# Revit family: QF_BOURGEAT_Self_5GN_et_6GN_vitrine_refrigeree_3nv
name_source: partatom
category: Equipement spécialisé
revit_build: Autodesk Revit 2015 (Build: 20140606_1530(x64)
units: mm (PartAtom-declared; Revit-internal decimal feet)

## types (36) — shared parameters
Certification = NF alimentaire
Charge max = 200.00 kg
Classe_climatique = 3
Fabricant = BOURGEAT
Fréquence = 50 Hz
Hauteur hors tout = 1800 mm  [stored 5.90551 ft]
Indice de protection = 21
Nature isolant = polyurethane
Niveau Sonore = 60dBa
Phase = 2
Profondeur hors tout = 820 mm  [stored 2.69029 ft]
Spécification du Fabricant = vitrine réfrigérée 3 niveaux OASIS
Tension = 230 V
Type Fluide Frigorigène = R404a
URL catalogue = http://www.bourgeat.fr

## per-type parameters (varying)
| type | Etageres | Intensité nominale | Longueur hors tout | Modèle | Pieds | Poids net à vide | Puissance frigorifique | Puissance électrique  | Roues | cuve_plate | lg_porte_groupe_froid | lg_vitrine | profondeur_cuve | reserve |
| 6GN_baie_libre_cuve_plate | Non | 11 A | 2335 mm  [stored 7.66076 ft] | 853106 | Oui | 380.00 kg | 2126W | 2500 W | Non | Oui | 790 mm  [stored 2.59186 ft] | 2200 mm | 0 mm  [stored 0 ft] | Non |
| 6GN_baie_libre_cuve90 | Non | 11 A | 2335 mm  [stored 7.66076 ft] | 853196 | Oui | 380.00 kg | 2126W | 2500 W | Non | Non | 790 mm  [stored 2.59186 ft] | 2200 mm | 90 mm  [stored 0.295276 ft] | Non |
| 6GN_reserve_cuve_plate | Non | 12 A | 2335 mm  [stored 7.66076 ft] | 853406 | Oui | 380.00 kg | 2126W | 2700 W | Non | Oui | 790 mm  [stored 2.59186 ft] | 2200 mm | 0 mm  [stored 0 ft] | Oui |
| 6GN_reserve_cuve90 | Non | 12 A | 2335 mm  [stored 7.66076 ft] | 853496 | Oui | 380.00 kg | 2126W | 2700 W | Non | Non | 790 mm  [stored 2.59186 ft] | 2200 mm | 90 mm  [stored 0.295276 ft] | Oui |
| 6GN_baie_libre_cuve_plate_roues | Non | 11 A | 2335 mm  [stored 7.66076 ft] | 853106 + 854950 | Non | 380.00 kg | 2126W | 2500 W | Oui | Oui | 790 mm  [stored 2.59186 ft] | 2200 mm | 0 mm  [stored 0 ft] | Non |
| 6GN_baie_libre_cuve90_roues | Non | 11 A | 2335 mm  [stored 7.66076 ft] | 853196 + 854950 | Non | 380.00 kg | 2126W | 2500 W | Oui | Non | 790 mm  [stored 2.59186 ft] | 2200 mm | 90 mm  [stored 0.295276 ft] | Non |
| 6GN_reserve_cuve_plate_roues | Non | 12 A | 2335 mm  [stored 7.66076 ft] | 853406 + 854950 | Non | 380.00 kg | 2126W | 2700 W | Oui | Oui | 790 mm  [stored 2.59186 ft] | 2200 mm | 0 mm  [stored 0 ft] | Oui |
| 6GN_reserve_cuve90_roues | Non | 12 A | 2335 mm  [stored 7.66076 ft] | 853496 + 854950 | Non | 380.00 kg | 2126W | 2700 W | Oui | Oui | 790 mm  [stored 2.59186 ft] | 2200 mm | 90 mm  [stored 0.295276 ft] | Oui |
| 6GN_baie_libre_cuve_plate_etageres | Oui | 11 A | 2335 mm  [stored 7.66076 ft] | 853106 + 854926 | Oui | 380.00 kg | 2126W | 2500 W | Non | Oui | 790 mm  [stored 2.59186 ft] | 2200 mm | 0 mm  [stored 0 ft] | Non |
| 6GN_baie_libre_cuve90_etageres | Oui | 11 A | 2335 mm  [stored 7.66076 ft] | 853196 + 854926 | Oui | 380.00 kg | 2126W | 2500 W | Non | Non | 790 mm  [stored 2.59186 ft] | 2200 mm | 90 mm  [stored 0.295276 ft] | Non |
| 6GN_baie_libre_cuve_plate_etageres_roues | Oui | 11 A | 2335 mm  [stored 7.66076 ft] | 853106 + 854926 + 854950 | Non | 380.00 kg | 2126W | 2500 W | Oui | Oui | 790 mm  [stored 2.59186 ft] | 2200 mm | 0 mm  [stored 0 ft] | Non |
| 6GN_baie_libre_cuve90_etageres_roues | Oui | 11 A | 2335 mm  [stored 7.66076 ft] | 853196 + 854926 + 854950 | Non | 380.00 kg | 2126W | 2500 W | Oui | Non | 790 mm  [stored 2.59186 ft] | 2200 mm | 90 mm  [stored 0.295276 ft] | Non |
| 5GN_baie_libre_cuve_plate | Non | 10 A | 2010 mm  [stored 6.59449 ft] | 853105 | Oui | 355.00 kg | 1440W | 2400 W | Non | Oui | 591 mm  [stored 1.93898 ft] | 1875 mm  [stored 6.15157 ft] | 0 mm  [stored 0 ft] | Non |
| 5GN_reserve_cuve_plate | Non | 11 A | 2010 mm  [stored 6.59449 ft] | 853405 | Oui | 355.00 kg | 1727W | 2500 W | Non | Oui | 591 mm  [stored 1.93898 ft] | 1875 mm  [stored 6.15157 ft] | 0 mm  [stored 0 ft] | Oui |
| 5GN_baie_libre_cuve90 | Non | 10 A | 2010 mm  [stored 6.59449 ft] | 853195 | Oui | 355.00 kg | 1440W | 2400 W | Non | Non | 591 mm  [stored 1.93898 ft] | 1875 mm  [stored 6.15157 ft] | 90 mm  [stored 0.295276 ft] | Non |
| 5GN_reserve_cuve90 | Non | 11 A | 2010 mm  [stored 6.59449 ft] | 853495 | Oui | 355.00 kg | 1727W | 2500 W | Non | Oui | 591 mm  [stored 1.93898 ft] | 1875 mm  [stored 6.15157 ft] | 90 mm  [stored 0.295276 ft] | Oui |
| 5GN_baie_libre_cuve_plate_roues | Non | 10 A | 2010 mm  [stored 6.59449 ft] | 853105 + 854950 | Non | 355.00 kg | 1440W | 2400 W | Oui | Oui | 591 mm  [stored 1.93898 ft] | 1875 mm  [stored 6.15157 ft] | 0 mm  [stored 0 ft] | Non |
| 5GN_baie_libre_cuve90_roues | Non | 10 A | 2010 mm  [stored 6.59449 ft] | 853195 + 854950 | Non | 355.00 kg | 1440W | 2400 W | Oui | Non | 591 mm  [stored 1.93898 ft] | 1875 mm  [stored 6.15157 ft] | 90 mm  [stored 0.295276 ft] | Non |
| 5GN_reserve_cuve_plate_roues | Non | 11 A | 2010 mm  [stored 6.59449 ft] | 853405 | Oui | 355.00 kg | 1727W | 2500 W | Non | Oui | 591 mm  [stored 1.93898 ft] | 1875 mm  [stored 6.15157 ft] | 0 mm  [stored 0 ft] | Oui |
| 5GN_reserve_cuve90_roues | Non | 11 A | 2010 mm  [stored 6.59449 ft] | 853495 + 854950 | Non | 355.00 kg | 1727W | 2500 W | Oui | Non | 591 mm  [stored 1.93898 ft] | 1875 mm  [stored 6.15157 ft] | 90 mm  [stored 0.295276 ft] | Oui |
| 5GN_baie_libre_cuve_plate_etageres | Oui | 10 A | 2010 mm  [stored 6.59449 ft] | 853105 + 854925 | Oui | 355.00 kg | 1440W | 2400 W | Non | Oui | 591 mm  [stored 1.93898 ft] | 1875 mm  [stored 6.15157 ft] | 0 mm  [stored 0 ft] | Non |
| 5GN_baie_libre_cuve90_etageres | Oui | 10 A | 2010 mm  [stored 6.59449 ft] | 853195 + 854925 | Oui | 355.00 kg | 1440W | 2400 W | Non | Non | 591 mm  [stored 1.93898 ft] | 1875 mm  [stored 6.15157 ft] | 90 mm  [stored 0.295276 ft] | Non |
| 5GN_baie_libre_cuve_plate_etageres_roues | Oui | 10 A | 2010 mm  [stored 6.59449 ft] | 853105 + 854925 + 854950 | Non | 355.00 kg | 1440W | 2400 W | Oui | Oui | 591 mm  [stored 1.93898 ft] | 1875 mm  [stored 6.15157 ft] | 0 mm  [stored 0 ft] | Non |
| 5GN_baie_libre_cuve90_etageres_roues | Oui | 10 A | 2010 mm  [stored 6.59449 ft] | 853195 + 854925 | Non | 355.00 kg | 1440W | 2400 W | Oui | Non | 591 mm  [stored 1.93898 ft] | 1875 mm  [stored 6.15157 ft] | 90 mm  [stored 0.295276 ft] | Non |
| 5GN_baie_libre_cuve_30 | Non | 10 A | 2010 mm  [stored 6.59449 ft] | 853205 | Oui | 355.00 kg | 1440W | 2400 W | Non | Oui | 591 mm  [stored 1.93898 ft] | 1875 mm  [stored 6.15157 ft] | 30 mm  [stored 0.0984252 ft] | Non |
| 5GN_baie_libre_cuve_30_etageres | Oui | 10 A | 2010 mm  [stored 6.59449 ft] | 853205 + 854925 | Oui | 355.00 kg | 1440W | 2400 W | Non | Oui | 591 mm  [stored 1.93898 ft] | 1875 mm  [stored 6.15157 ft] | 30 mm  [stored 0.0984252 ft] | Non |
| 5GN_baie_libre_cuve_30_etageres_roues | Oui | 10 A | 2010 mm  [stored 6.59449 ft] | 853205 + 854925 + 854950 | Non | 355.00 kg | 1440W | 2400 W | Oui | Oui | 591 mm  [stored 1.93898 ft] | 1875 mm  [stored 6.15157 ft] | 30 mm  [stored 0.0984252 ft] | Non |
| 5GN_baie_libre_cuve_30_roues | Non | 10 A | 2010 mm  [stored 6.59449 ft] | 853205 + 854950 | Non | 355.00 kg | 1440W | 2400 W | Oui | Oui | 591 mm  [stored 1.93898 ft] | 1875 mm  [stored 6.15157 ft] | 30 mm  [stored 0.0984252 ft] | Non |
| 5GN_reserve_cuve_30 | Non | 11 A | 2010 mm  [stored 6.59449 ft] | 853605 | Oui | 355.00 kg | 1727W | 2500 W | Non | Oui | 591 mm  [stored 1.93898 ft] | 1875 mm  [stored 6.15157 ft] | 30 mm  [stored 0.0984252 ft] | Oui |
| 5GN_reserve_cuve_30_roues | Non | 11 A | 2010 mm  [stored 6.59449 ft] | 853605 | Oui | 355.00 kg | 1727W | 2500 W | Non | Oui | 591 mm  [stored 1.93898 ft] | 1875 mm  [stored 6.15157 ft] | 30 mm  [stored 0.0984252 ft] | Oui |
| 6GN_baie_libre_cuve_30 | Non | 11 A | 2335 mm  [stored 7.66076 ft] | 853206 | Oui | 380.00 kg | 2126W | 2500 W | Non | Oui | 790 mm  [stored 2.59186 ft] | 2200 mm | 30 mm  [stored 0.0984252 ft] | Non |
| 6GN_baie_libre_cuve_30_etageres | Oui | 11 A | 2335 mm  [stored 7.66076 ft] | 853606 + 854926 | Oui | 380.00 kg | 2126W | 2500 W | Non | Oui | 790 mm  [stored 2.59186 ft] | 2200 mm | 30 mm  [stored 0.0984252 ft] | Non |
| 6GN_baie_libre_cuve_30_etageres_roues | Oui | 11 A | 2335 mm  [stored 7.66076 ft] | 853206 + 854926 + 854950 | Non | 380.00 kg | 2126W | 2500 W | Oui | Oui | 790 mm  [stored 2.59186 ft] | 2200 mm | 30 mm  [stored 0.0984252 ft] | Non |
| 6GN_baie_libre_cuve_30_roues | Non | 11 A | 2335 mm  [stored 7.66076 ft] | 853206 + 854950 | Non | 380.00 kg | 2126W | 2500 W | Oui | Oui | 790 mm  [stored 2.59186 ft] | 2200 mm | 30 mm  [stored 0.0984252 ft] | Non |
| 6GN_reserve_cuve_30 | Non | 12 A | 2335 mm  [stored 7.66076 ft] | 853606 | Oui | 380.00 kg | 2126W | 2700 W | Non | Oui | 790 mm  [stored 2.59186 ft] | 2200 mm | 30 mm  [stored 0.0984252 ft] | Oui |
| 6GN_reserve_cuve_30_roues | Non | 12 A | 2335 mm  [stored 7.66076 ft] | 853606 + 854950 | Non | 380.00 kg | 2126W | 2700 W | Oui | Oui | 790 mm  [stored 2.59186 ft] | 2200 mm | 30 mm  [stored 0.0984252 ft] | Oui |

note: [stored X ft] marks values corroborated as IEEE doubles in the binary element streams (Revit-internal decimal feet)

## geometry (parser evidence)
native form markers: Blend x6
no freeform markers — native parametric forms only
